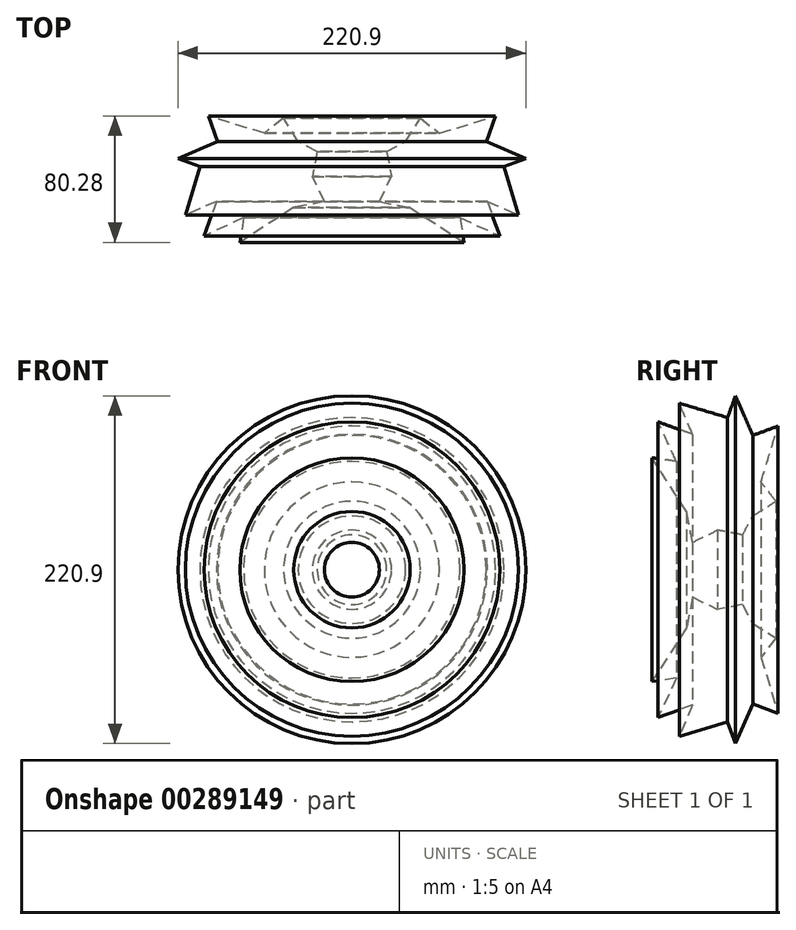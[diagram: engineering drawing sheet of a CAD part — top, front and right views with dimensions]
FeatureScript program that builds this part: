
annotation { "Feature Type Name" : "Feature", "Feature Type Description" : "" }
export const myFeature = defineFeature(function(context is Context, id is Id, definition is map)
    precondition{}
    {
        {
            var Q0;
            Q0=qCreatedBy(makeId("Top.planeOp"),FACE);
            var sketch = newSketch(context, id + "F0", { "sketchPlane" : qUnion([Q0])});
            skLineSegment(sketch, "E0", {"start": v(-44.54, 11.94) * mm, "end": v(-32.5, 18.4) * mm});
            skLineSegment(sketch, "E1", {"start": v(-32.5, 18.4) * mm, "end": v(-23.17, 33.13) * mm});
            skLineSegment(sketch, "E2", {"start": v(-23.17, 33.13) * mm, "end": v(-10.95, 23.62) * mm});
            skLineSegment(sketch, "E3", {"start": v(-10.95, 23.62) * mm, "end": v(24.6, 34.57) * mm});
            skLineSegment(sketch, "E4", {"start": v(24.6, 34.57) * mm, "end": v(18.68, 18.4) * mm});
            skLineSegment(sketch, "E5", {"start": v(18.68, 18.4) * mm, "end": v(43.82, 7.45) * mm});
            skLineSegment(sketch, "E6", {"start": v(43.82, 7.45) * mm, "end": v(30, 2.42) * mm});
            skLineSegment(sketch, "E7", {"start": v(30, 2.42) * mm, "end": v(39.15, -28.29) * mm});
            skLineSegment(sketch, "E8", {"start": v(39.15, -28.29) * mm, "end": v(19.4, -19.84) * mm});
            skLineSegment(sketch, "E9", {"start": v(19.4, -19.84) * mm, "end": v(27.3, -41.75) * mm});
            skLineSegment(sketch, "E10", {"start": v(27.3, -41.75) * mm, "end": v(2.16, -30.08) * mm});
            skLineSegment(sketch, "E11", {"start": v(2.16, -30.08) * mm, "end": v(4.49, -45.7) * mm});
            skLineSegment(sketch, "E12", {"start": v(4.49, -45.7) * mm, "end": v(-29.63, -23.62) * mm});
            skLineSegment(sketch, "E13", {"start": v(-29.63, -23.62) * mm, "end": v(-49.2, -19.84) * mm});
            skLineSegment(sketch, "E14", {"start": v(-49.2, -19.84) * mm, "end": v(-41.49, -3.86) * mm});
            skLineSegment(sketch, "E15", {"start": v(-41.49, -3.86) * mm, "end": v(-44.54, 11.94) * mm});
            skLineSegment(sketch, "E16", {"start": v(-66.63, 12.84) * mm, "end": v(-66.63, -20.38) * mm});
            skSolve(sketch);
        }
        {
            var Q0;
            Q0=makeQuery(id+"F0.imprint","IMPRINT",FACE,{"disambiguationData":[TD([[makeQuery(id+"F0.imprint","IMPRINT",EDGE,{"derivedFrom":sQuery(id+"F0.wireOp",EDGE,"E0")}),-1.0]])]});
            var Q1;
            Q1=sQuery(id+"F0.wireOp",EDGE,"E16");
            revolve(context, id + "F1", {"entities" : qUnion([Q0]), "axis" : qUnion([Q1]), "revolveType" : RevolveType.FULL});
        }
    });
